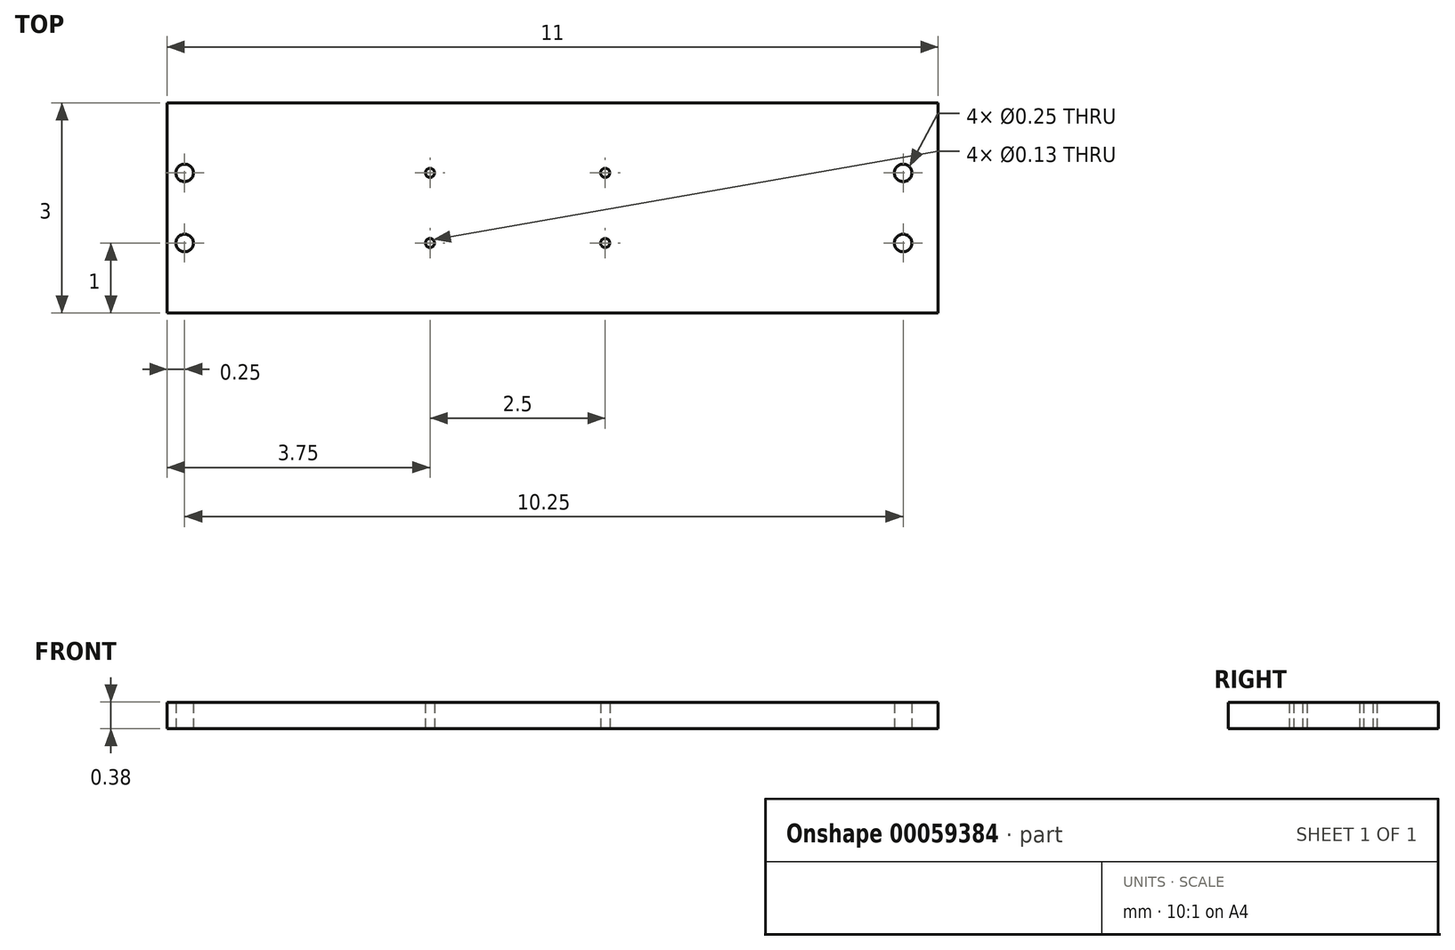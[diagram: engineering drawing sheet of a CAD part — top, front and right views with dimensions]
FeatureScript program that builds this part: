
annotation { "Feature Type Name" : "Feature", "Feature Type Description" : "" }
export const myFeature = defineFeature(function(context is Context, id is Id, definition is map)
    precondition{}
    {
        {
            var Q0;
            Q0=qCreatedBy(makeId("Top.planeOp"),FACE);
            var sketch = newSketch(context, id + "F0", { "sketchPlane" : qUnion([Q0])});
            skLineSegment(sketch, "E0.rect.bottom", {"start": v(5.5, 1.5) * mm, "end": v(-5.5, 1.5) * mm});
            skLineSegment(sketch, "E0.rect.top", {"start": v(5.5, -1.5) * mm, "end": v(-5.5, -1.5) * mm});
            skLineSegment(sketch, "E0.rect.left", {"start": v(5.5, 1.5) * mm, "end": v(5.5, -1.5) * mm});
            skLineSegment(sketch, "E0.rect.right", {"start": v(-5.5, 1.5) * mm, "end": v(-5.5, -1.5) * mm});
            skPoint(sketch, "E0.rect.middle", {"position": v(0, 0) * mm});
            skCircle(sketch, "E1", {"center": v(5, 0.5) * mm, "radius": 0.12 * mm});
            skCircle(sketch, "E2", {"center": v(5, -0.5) * mm, "radius": 0.12 * mm});
            skCircle(sketch, "E3", {"center": v(0.75, 0.5) * mm, "radius": 0.07 * mm});
            skCircle(sketch, "E4", {"center": v(0.75, -0.5) * mm, "radius": 0.07 * mm});
            skCircle(sketch, "E5", {"center": v(-1.75, -0.5) * mm, "radius": 0.07 * mm});
            skCircle(sketch, "E6", {"center": v(-1.75, 0.5) * mm, "radius": 0.07 * mm});
            skCircle(sketch, "E7", {"center": v(-5.25, 0.5) * mm, "radius": 0.12 * mm});
            skCircle(sketch, "E8", {"center": v(-5.25, -0.5) * mm, "radius": 0.12 * mm});
            skSolve(sketch);
        }
        {
            var Q0;
            Q0=makeQuery(id+"F0.imprint","IMPRINT",FACE,{"disambiguationData":[TD([[makeQuery(id+"F0.imprint","IMPRINT",EDGE,{"derivedFrom":sQuery(id+"F0.wireOp",EDGE,"E0.rect.bottom")}),1.0]])]});
            extrude(context, id + "F1", {"entities" : qUnion([Q0]), "depth" : .375 * mm});
        }
    });
